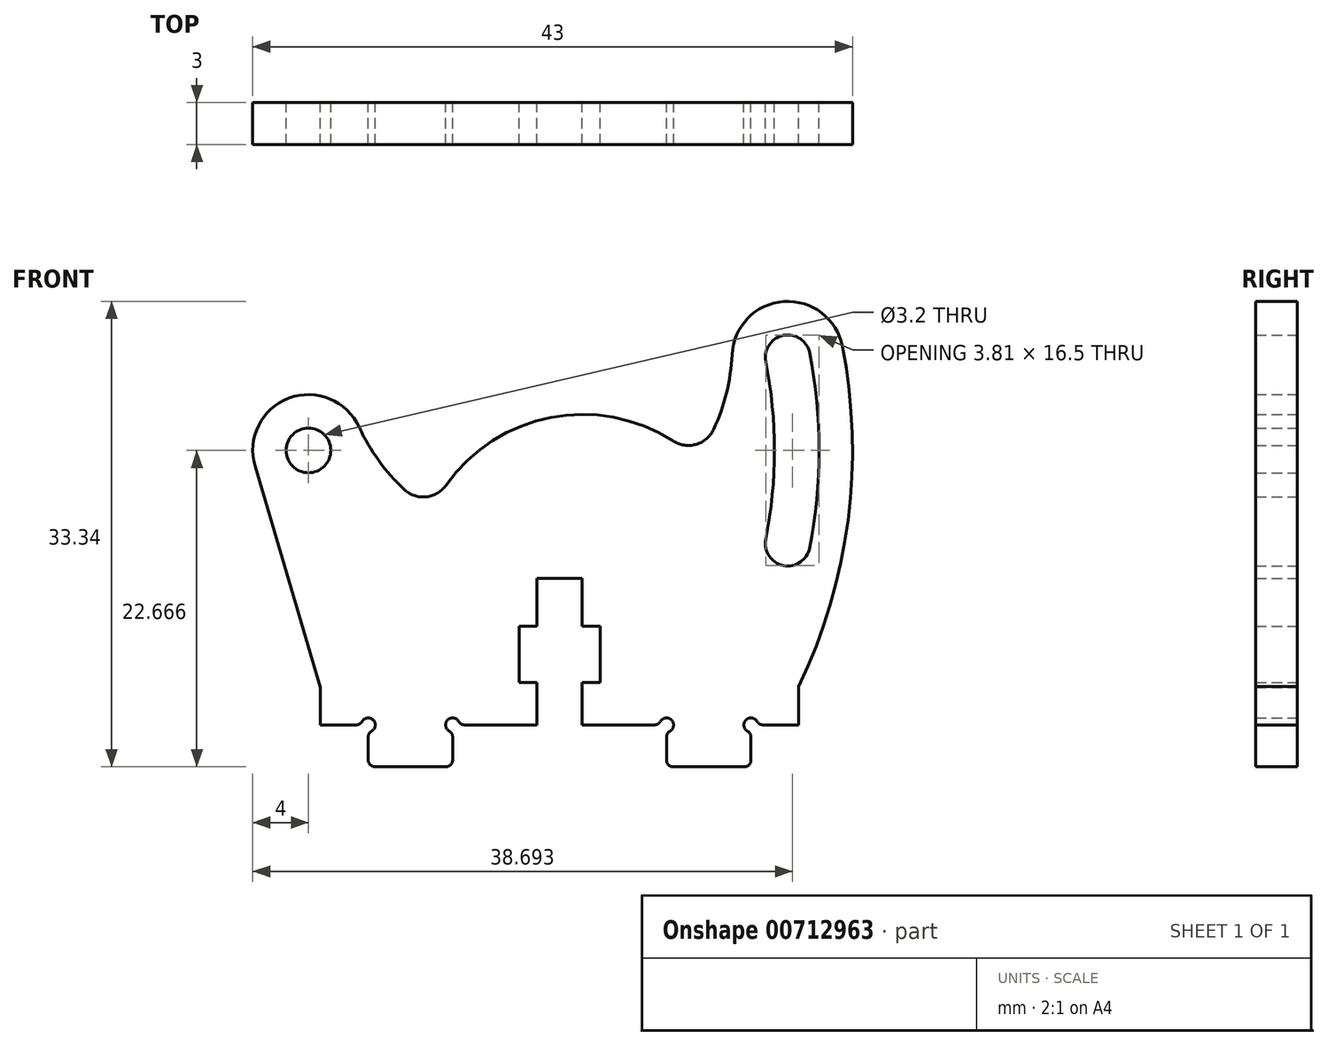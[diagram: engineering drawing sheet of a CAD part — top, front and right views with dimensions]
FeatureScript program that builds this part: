
annotation { "Feature Type Name" : "Feature", "Feature Type Description" : "" }
export const myFeature = defineFeature(function(context is Context, id is Id, definition is map)
    precondition{}
    {
        {
            var Q0;
            Q0=qCreatedBy(makeId("Front.planeOp"),FACE);
            var sketch = newSketch(context, id + "F0", { "sketchPlane" : qUnion([Q0])});
            skArc(sketch, "E0", {"start": v(-13.86, 7.66) * mm, "mid": v(-12.47, 5.26) * mm, "end": v(-10.63, 3.19) * mm});
            skArc(sketch, "E1", {"start": v(-13.86, 7.66) * mm, "mid": v(-18.9, 9.74) * mm, "end": v(-21.34, 4.86) * mm});
            skLineSegment(sketch, "E2", {"start": v(-21.34, 4.86) * mm, "end": v(-16.65, -11) * mm});
            skLineSegment(sketch, "E3", {"start": v(-16.65, -11) * mm, "end": v(-16.65, -13.67) * mm});
            skLineSegment(sketch, "E4", {"start": v(-16.65, -13.67) * mm, "end": v(-14.1, -13.67) * mm});
            skArc(sketch, "E5", {"start": v(-14.1, -13.67) * mm, "mid": v(-13.84, -13.6) * mm, "end": v(-13.66, -13.42) * mm});
            skArc(sketch, "E6", {"start": v(-12.97, -14.11) * mm, "mid": v(-12.86, -13.32) * mm, "end": v(-13.66, -13.42) * mm});
            skArc(sketch, "E7", {"start": v(-12.97, -14.11) * mm, "mid": v(-13.15, -14.3) * mm, "end": v(-13.22, -14.55) * mm});
            skLineSegment(sketch, "E8", {"start": v(-13.22, -14.55) * mm, "end": v(-13.22, -16.17) * mm});
            skArc(sketch, "E9", {"start": v(-13.22, -16.17) * mm, "mid": v(-13.07, -16.53) * mm, "end": v(-12.72, -16.67) * mm});
            skLineSegment(sketch, "E10", {"start": v(-12.72, -16.67) * mm, "end": v(-7.67, -16.67) * mm});
            skArc(sketch, "E11", {"start": v(-7.67, -16.67) * mm, "mid": v(-7.31, -16.53) * mm, "end": v(-7.17, -16.17) * mm});
            skLineSegment(sketch, "E12", {"start": v(-7.17, -16.17) * mm, "end": v(-7.17, -14.55) * mm});
            skArc(sketch, "E13", {"start": v(-7.17, -14.55) * mm, "mid": v(-7.23, -14.3) * mm, "end": v(-7.42, -14.11) * mm});
            skArc(sketch, "E14", {"start": v(-6.73, -13.42) * mm, "mid": v(-7.52, -13.32) * mm, "end": v(-7.42, -14.11) * mm});
            skArc(sketch, "E15", {"start": v(-6.73, -13.42) * mm, "mid": v(-6.54, -13.6) * mm, "end": v(-6.3, -13.67) * mm});
            skLineSegment(sketch, "E16", {"start": v(-6.3, -13.67) * mm, "end": v(-1.11, -13.67) * mm});
            skLineSegment(sketch, "E17", {"start": v(-1.11, -13.67) * mm, "end": v(-1.11, -10.65) * mm});
            skLineSegment(sketch, "E18", {"start": v(-1.11, -10.65) * mm, "end": v(-2.4, -10.65) * mm});
            skLineSegment(sketch, "E19", {"start": v(-2.4, -10.65) * mm, "end": v(-2.4, -6.61) * mm});
            skLineSegment(sketch, "E20", {"start": v(-2.4, -6.61) * mm, "end": v(-1.11, -6.61) * mm});
            skLineSegment(sketch, "E21", {"start": v(-1.11, -6.61) * mm, "end": v(-1.11, -3.17) * mm});
            skLineSegment(sketch, "E22", {"start": v(-1.11, -3.17) * mm, "end": v(2.11, -3.17) * mm});
            skLineSegment(sketch, "E23", {"start": v(2.11, -3.17) * mm, "end": v(2.11, -6.61) * mm});
            skLineSegment(sketch, "E24", {"start": v(2.11, -6.61) * mm, "end": v(3.4, -6.61) * mm});
            skLineSegment(sketch, "E25", {"start": v(3.4, -6.61) * mm, "end": v(3.4, -10.65) * mm});
            skLineSegment(sketch, "E26", {"start": v(3.4, -10.65) * mm, "end": v(2.11, -10.65) * mm});
            skLineSegment(sketch, "E27", {"start": v(2.11, -10.65) * mm, "end": v(2.11, -13.67) * mm});
            skLineSegment(sketch, "E28", {"start": v(2.11, -13.67) * mm, "end": v(7.3, -13.67) * mm});
            skArc(sketch, "E29", {"start": v(7.3, -13.67) * mm, "mid": v(7.54, -13.6) * mm, "end": v(7.73, -13.42) * mm});
            skArc(sketch, "E30", {"start": v(8.42, -14.11) * mm, "mid": v(8.52, -13.32) * mm, "end": v(7.73, -13.42) * mm});
            skArc(sketch, "E31", {"start": v(8.42, -14.11) * mm, "mid": v(8.23, -14.3) * mm, "end": v(8.17, -14.55) * mm});
            skLineSegment(sketch, "E32", {"start": v(8.17, -14.55) * mm, "end": v(8.17, -16.17) * mm});
            skArc(sketch, "E33", {"start": v(8.17, -16.17) * mm, "mid": v(8.31, -16.53) * mm, "end": v(8.67, -16.67) * mm});
            skLineSegment(sketch, "E34", {"start": v(8.67, -16.67) * mm, "end": v(13.72, -16.67) * mm});
            skArc(sketch, "E35", {"start": v(13.72, -16.67) * mm, "mid": v(14.07, -16.53) * mm, "end": v(14.22, -16.17) * mm});
            skLineSegment(sketch, "E36", {"start": v(14.22, -16.17) * mm, "end": v(14.22, -14.55) * mm});
            skArc(sketch, "E37", {"start": v(14.22, -14.55) * mm, "mid": v(14.15, -14.3) * mm, "end": v(13.97, -14.11) * mm});
            skArc(sketch, "E38", {"start": v(14.66, -13.42) * mm, "mid": v(13.86, -13.32) * mm, "end": v(13.97, -14.11) * mm});
            skArc(sketch, "E39", {"start": v(14.66, -13.42) * mm, "mid": v(14.84, -13.6) * mm, "end": v(15.1, -13.67) * mm});
            skLineSegment(sketch, "E40", {"start": v(15.1, -13.67) * mm, "end": v(17.65, -13.67) * mm});
            skLineSegment(sketch, "E41", {"start": v(17.65, -13.67) * mm, "end": v(17.65, -11) * mm});
            skArc(sketch, "E42", {"start": v(17.65, -11) * mm, "mid": v(17.65, -10.95) * mm, "end": v(17.65, -10.9) * mm});
            skLineSegment(sketch, "E43", {"start": v(17.65, -10.9) * mm, "end": v(17.65, -10.9) * mm});
            skArc(sketch, "E44", {"start": v(17.65, -10.9) * mm, "mid": v(21.18, 1.01) * mm, "end": v(20.78, 13.44) * mm});
            skArc(sketch, "E45", {"start": v(20.78, 13.44) * mm, "mid": v(16.56, 16.66) * mm, "end": v(12.86, 12.85) * mm});
            skArc(sketch, "E46", {"start": v(11.54, 7.5) * mm, "mid": v(12.46, 10.1) * mm, "end": v(12.86, 12.85) * mm});
            skArc(sketch, "E47", {"start": v(8.65, 6.67) * mm, "mid": v(10.28, 6.43) * mm, "end": v(11.54, 7.5) * mm});
            skArc(sketch, "E48", {"start": v(8.65, 6.67) * mm, "mid": v(-0.13, 8.35) * mm, "end": v(-7.64, 3.5) * mm});
            skArc(sketch, "E49", {"start": v(-10.63, 3.19) * mm, "mid": v(-9.06, 2.67) * mm, "end": v(-7.64, 3.5) * mm});
            skArc(sketch, "E50", {"start": v(18.43, -0.99) * mm, "mid": v(19.1, 6) * mm, "end": v(18.43, 12.98) * mm});
            skArc(sketch, "E51", {"start": v(15.29, -0.38) * mm, "mid": v(16.55, -2.25) * mm, "end": v(18.43, -0.99) * mm});
            skArc(sketch, "E52", {"start": v(15.29, -0.38) * mm, "mid": v(15.9, 6) * mm, "end": v(15.29, 12.37) * mm});
            skArc(sketch, "E53", {"start": v(18.43, 12.98) * mm, "mid": v(16.55, 14.24) * mm, "end": v(15.29, 12.37) * mm});
            skCircle(sketch, "E54", {"center": v(-17.5, 6) * mm, "radius": 1.6 * mm});
            skLineSegment(sketch, "E55", {"start": v(0.5, -3.17) * mm, "end": v(0.5, -17.13) * mm, "construction": true});
            skSolve(sketch);
        }
        {
            var Q0;
            Q0=qSketchRegion(id+"F0",true);
            extrude(context, id + "F1", {"entities" : qUnion([Q0]), "depth" : 3 * mm, "offsetDistance" : 25 * mm});
        }
    });
